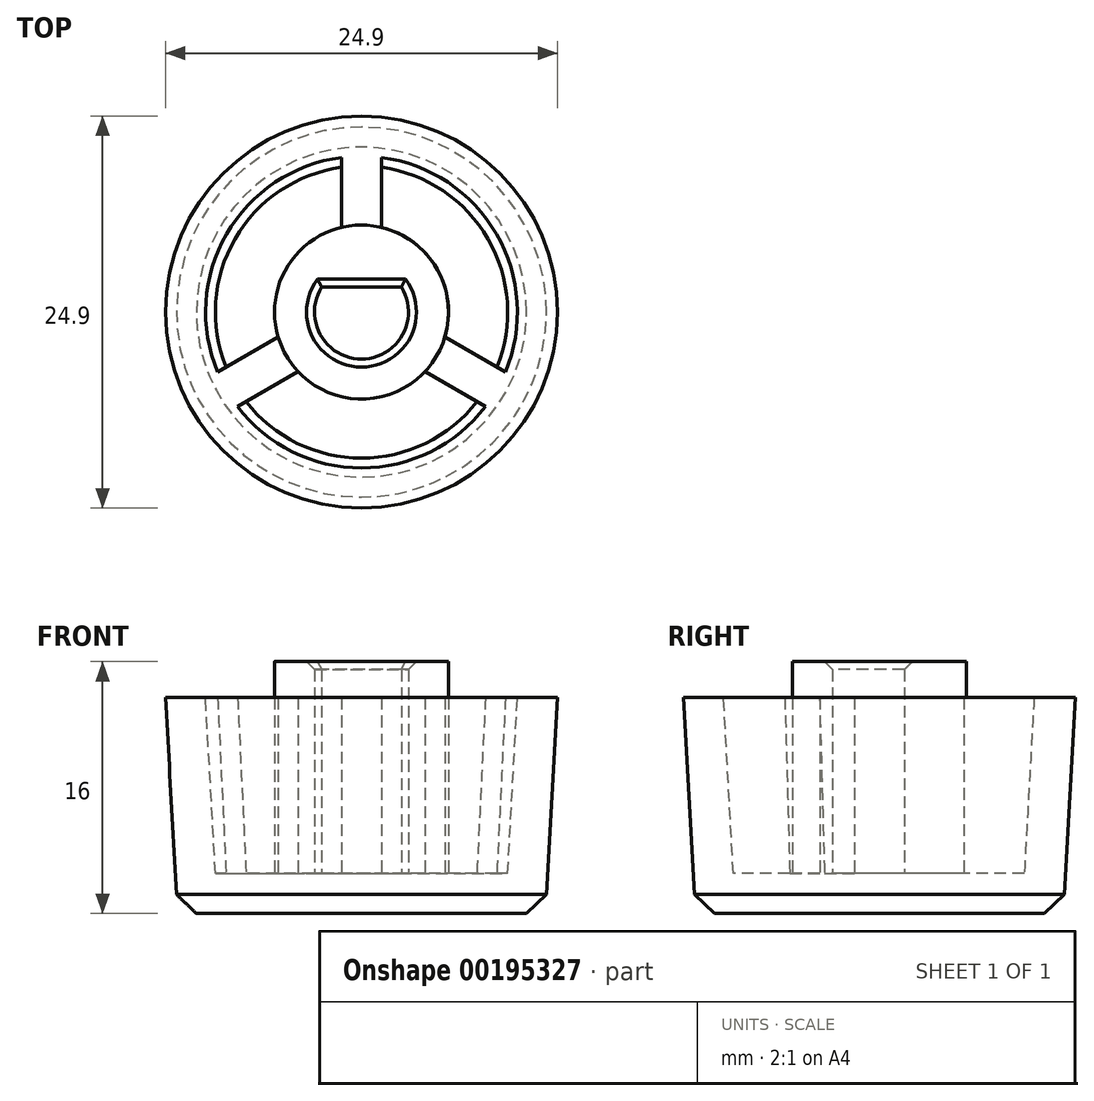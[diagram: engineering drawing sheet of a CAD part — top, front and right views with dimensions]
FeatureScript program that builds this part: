
annotation { "Feature Type Name" : "Feature", "Feature Type Description" : "" }
export const myFeature = defineFeature(function(context is Context, id is Id, definition is map)
    precondition{}
    {
        {
            var Q0;
            Q0=qCreatedBy(makeId("Front.planeOp"),FACE);
            var sketch = newSketch(context, id + "F0", { "sketchPlane" : qUnion([Q0])});
            skLineSegment(sketch, "E0", {"start": v(0, 0) * mm, "end": v(11.68, 0) * mm});
            skLineSegment(sketch, "E1", {"start": v(11.68, 0) * mm, "end": v(12.45, 13.72) * mm});
            skLineSegment(sketch, "E2", {"start": v(0, 0) * mm, "end": v(0, 2.54) * mm});
            skLineSegment(sketch, "E3", {"start": v(0, 2.54) * mm, "end": v(9.28, 2.54) * mm});
            skLineSegment(sketch, "E4", {"start": v(9.28, 2.54) * mm, "end": v(9.9, 13.72) * mm});
            skLineSegment(sketch, "E5", {"start": v(9.9, 13.72) * mm, "end": v(12.45, 13.72) * mm});
            skSolve(sketch);
        }
        {
            var Q0;
            Q0 = qSketchRegion(id + "F0", true);
            var Q1;
            Q1=sQuery(id+"F0.wireOp",EDGE,"E2");
            revolve(context, id + "F1", {"entities" : qUnion([Q0]), "axis" : qUnion([Q1]), "revolveType" : RevolveType.FULL});
        }
        {
            var Q0;
            Q0=makeQuery(id+"F1.opRevolve","SWEPT_FACE",FACE,{"disambiguationData":[OSD([sQuery(id+"F0.wireOp",EDGE,"E3")])]});
            var sketch = newSketch(context, id + "F2", { "sketchPlane" : qUnion([Q0])});
            skCircle(sketch, "E6", {"center": v(0, 0) * mm, "radius": 5.52 * mm});
            skLineSegment(sketch, "E7", {"start": v(-2.53, 1.59) * mm, "end": v(2.53, 1.59) * mm});
            skPoint(sketch, "E8", {"position": v(0.03, -2.98) * mm});
            skArc(sketch, "E9", {"start": v(-2.53, 1.59) * mm, "mid": v(0, -2.98) * mm, "end": v(2.53, 1.59) * mm});
            skSolve(sketch);
        }
        {
            var Q0;
            Q0=makeQuery(id+"F2.imprint","IMPRINT",FACE,{"disambiguationData":[TD([[makeQuery(id+"F2.imprint","IMPRINT",EDGE,{"derivedFrom":sQuery(id+"F2.wireOp",EDGE,"E6")}),1.0]])]});
            extrude(context, id + "F3", {"entities" : qUnion([Q0]), "operationType" : NewBodyOperationType.ADD, "depth" : 13.46 * mm});
        }
        {
            var Q0;
            Q0=makeQuery(id+"F3.boolean.opBoolean","SPLIT",FACE,{"disambiguationData":[TD([makeQuery(id+"F1.opRevolve","SWEPT_FACE",FACE,{"disambiguationData":[OSD([sQuery(id+"F0.wireOp",EDGE,"E4")])]})])],"derivedFrom":makeQuery(id+"F1.opRevolve","SWEPT_FACE",FACE,{"disambiguationData":[OSD([sQuery(id+"F0.wireOp",EDGE,"E3")])]})});
            var sketch = newSketch(context, id + "F4", { "sketchPlane" : qUnion([Q0])});
            skLineSegment(sketch, "E10.bottom", {"start": v(-1.27, 10.92) * mm, "end": v(1.27, 10.92) * mm});
            skLineSegment(sketch, "E10.top", {"start": v(-1.27, 5.08) * mm, "end": v(1.27, 5.08) * mm});
            skLineSegment(sketch, "E10.left", {"start": v(-1.27, 10.92) * mm, "end": v(-1.27, 5.08) * mm});
            skLineSegment(sketch, "E10.right", {"start": v(1.27, 10.92) * mm, "end": v(1.27, 5.08) * mm});
            skLineSegment(sketch, "E11.1.0", {"start": v(-8.82, -6.56) * mm, "end": v(-3.76, -3.64) * mm});
            skLineSegment(sketch, "E11.1.1", {"start": v(-8.82, -6.56) * mm, "end": v(-10.1, -4.36) * mm});
            skLineSegment(sketch, "E11.1.2", {"start": v(-10.1, -4.36) * mm, "end": v(-5.03, -1.44) * mm});
            skLineSegment(sketch, "E11.1.3", {"start": v(-3.76, -3.64) * mm, "end": v(-5.03, -1.44) * mm});
            skLineSegment(sketch, "E11.2.0", {"start": v(10.1, -4.36) * mm, "end": v(5.03, -1.44) * mm});
            skLineSegment(sketch, "E11.2.1", {"start": v(10.1, -4.36) * mm, "end": v(8.82, -6.56) * mm});
            skLineSegment(sketch, "E11.2.2", {"start": v(8.82, -6.56) * mm, "end": v(3.76, -3.64) * mm});
            skLineSegment(sketch, "E11.2.3", {"start": v(5.03, -1.44) * mm, "end": v(3.76, -3.64) * mm});
            skPoint(sketch, "E11.center", {"position": v(0, 0) * mm});
            skSolve(sketch);
        }
        {
            var Q0;
            Q0 = qSketchRegion(id + "F4", true);
            var Q1;
            Q1=makeQuery(id+"F1.opRevolve","SWEPT_FACE",FACE,{"disambiguationData":[OSD([sQuery(id+"F0.wireOp",EDGE,"E5")])]});
            extrude(context, id + "F5", {"entities" : qUnion([Q0]), "operationType" : NewBodyOperationType.ADD, "endBound" : BoundingType.UP_TO_SURFACE, "endBoundEntityFace" : qUnion([Q1]), "depth" : 25.4 * mm});
        }
        {
            var Q0;
            Q0=makeQuery(id+"F3.opExtrude","CAP_EDGE",EDGE,{"disambiguationData":[OSD([sQuery(id+"F2.wireOp",EDGE,"E7")])],"isStart":false});
            var Q1;
            Q1=makeQuery(id+"F3.opExtrude","CAP_EDGE",EDGE,{"disambiguationData":[OSD([sQuery(id+"F2.wireOp",EDGE,"E9")])],"isStart":false});
            chamfer(context, id + "F6", {"entities" : qUnion([Q0, Q1]), "width" : 0.5 * mm, "tangentPropagation" : true});
        }
        {
            var Q0;
            Q0=makeQuery(id+"F1.opRevolve","SWEPT_EDGE",EDGE,{"disambiguationData":[OSD([sQuery(id+"F0.wireOp",EDGE,"E0"),sQuery(id+"F0.wireOp",EDGE,"E1")])]});
            chamfer(context, id + "F7", {"entities" : qUnion([Q0]), "width" : 1.27 * mm, "tangentPropagation" : true});
        }
    });
